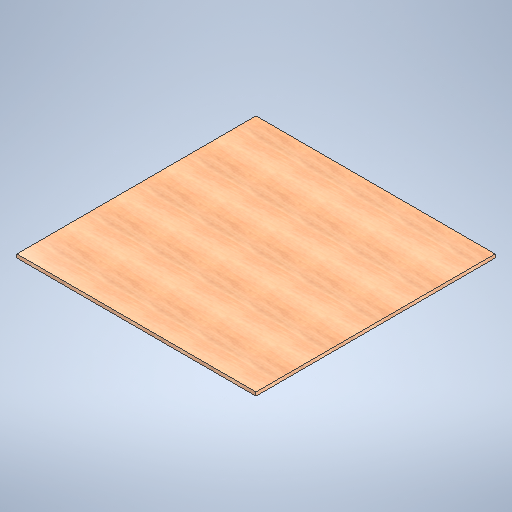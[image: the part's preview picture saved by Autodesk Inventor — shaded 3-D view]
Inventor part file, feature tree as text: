
AUTODESK INVENTOR PART (.ipt)
format: ipt  version: 2025 (Build 290162010, 162A)  size: 333,824 bytes
history: native  units: in
note: dims shown in document units (in); Inventor stores cm internally (conversion verified against a paired STEP export)
features: extrude x1, sketch x1
ambient origin geometry x8: Origin, YZ Plane, XZ Plane, XY Plane, X Axis, Y Axis, Z Axis, Center Point
bodies: Solid1 (feature_tree)
feature tree (2):
  extrude  "Extrusion1"  Depth=48.0in
  sketch  "Sketch1"  dims[d2=48.0in d3=48.0in d4=0.7188in d5=0.0in]
